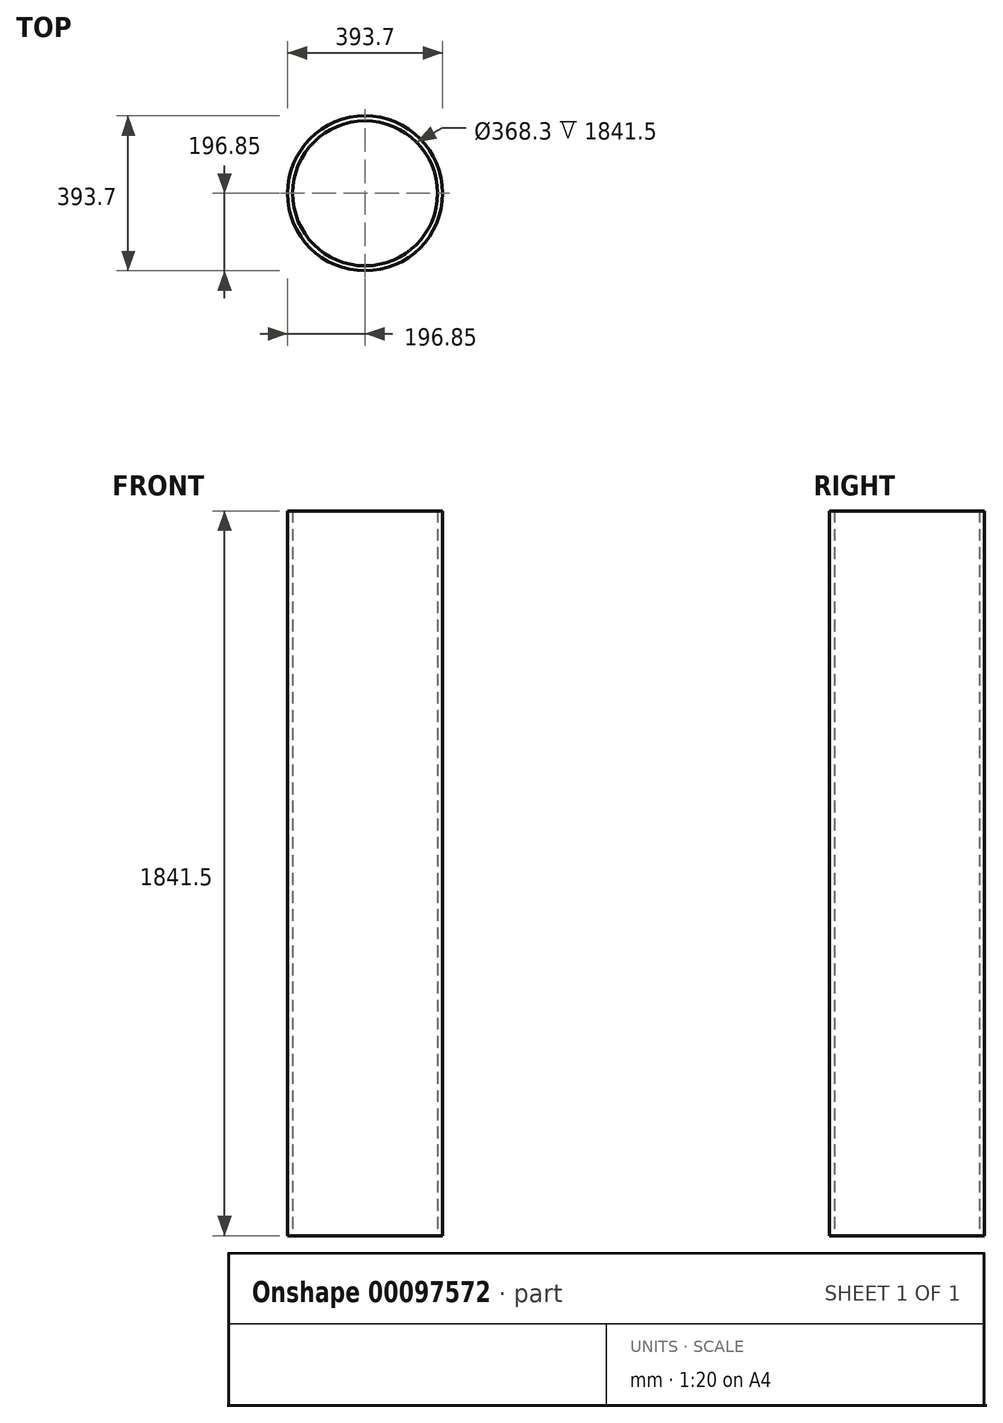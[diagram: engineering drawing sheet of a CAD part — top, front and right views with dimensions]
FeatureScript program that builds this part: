
annotation { "Feature Type Name" : "Feature", "Feature Type Description" : "" }
export const myFeature = defineFeature(function(context is Context, id is Id, definition is map)
    precondition{}
    {
        {
            var Q0;
            Q0=qCreatedBy(makeId("Top.planeOp"),FACE);
            var sketch = newSketch(context, id + "F0", { "sketchPlane" : qUnion([Q0])});
            skCircle(sketch, "E0", {"center": v(0, 0) * mm, "radius": 196.85 * mm});
            skCircle(sketch, "E1", {"center": v(0, 0) * mm, "radius": 184.15 * mm});
            skSolve(sketch);
        }
        {
            var Q0;
            Q0 = qSketchRegion(id + "F0", true);
            extrude(context, id + "F1", {"entities" : qUnion([Q0]), "depth" : 1841.5 * mm, "offsetDistance" : 25.4 * mm});
        }
    });
